# Revit family: Haworth_BuzziHub_Table_Collaborative
name_source: partatom
category: Furniture
revit_build: Autodesk Revit 2018 (Build: 20170223_1515(x64)
units: mm (PartAtom-declared; Revit-internal decimal feet)

## family parameters
Always vertical = Yes
Cut with Voids When Loaded = No
OmniClass Number = 23.40.70.14.64.21
OmniClass Title = Systems Furniture
Room Calculation Point = No
Shared = No
Work Plane-Based = No

## types (2) — shared parameters
Actual Depth = 31 1/2"
Actual Width = 74 105/256"
Assembly Code = E2020200
Manufacturer = Haworth
Model = HCBZ-HBTC
Revision Number = 1
Size = Verify Final Dim. w/ Haworth
URL = http://www.haworth.com
URL - Product = https://www.haworth.com
Warranty = http://www.haworth.com

## per-type parameters (varying)
| type | Actual Height | Bar Height | Description | Standard Height |
| HCBZ-HBTC-2 | 43 79/256" | Yes | Haworth BuzziHub Table Bar Height Collaborative Table | No |
| HCBZ-HBTC-1 | 29 17/32" | No | Haworth BuzziHub Table Standard Height Collaborative Table | Yes |

## geometry (parser evidence)
native form markers: Sweep x3
no freeform markers — native parametric forms only
